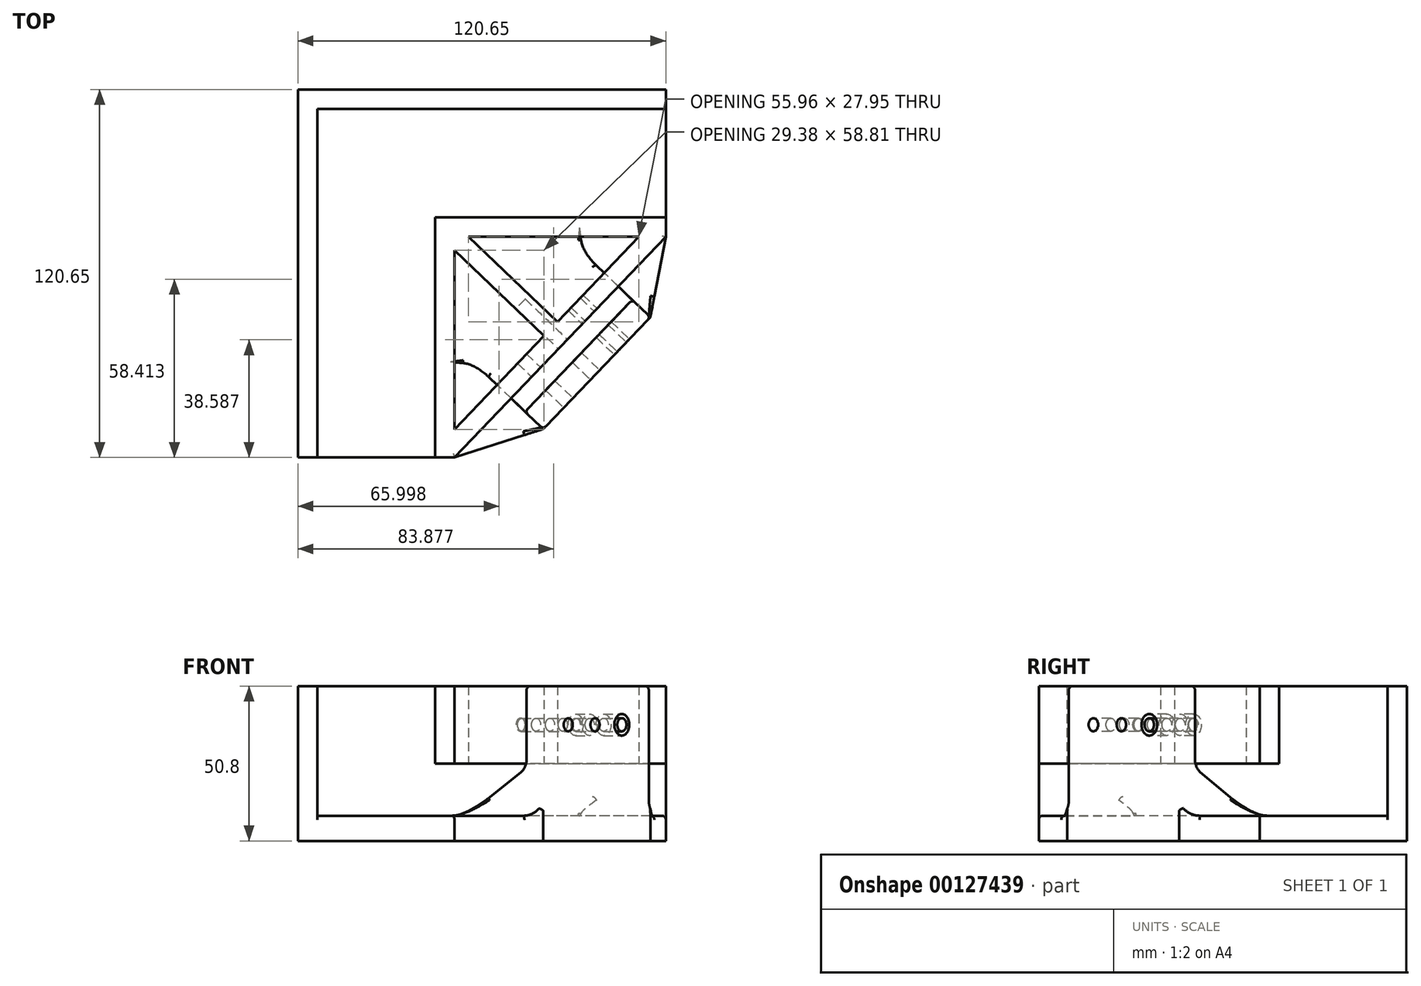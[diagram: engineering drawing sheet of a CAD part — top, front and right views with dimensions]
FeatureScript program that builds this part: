
annotation { "Feature Type Name" : "Feature", "Feature Type Description" : "" }
export const myFeature = defineFeature(function(context is Context, id is Id, definition is map)
    precondition{}
    {
        {
            var Q0;
            Q0=qCreatedBy(makeId("Top.planeOp"),FACE);
            var sketch = newSketch(context, id + "F0", { "sketchPlane" : qUnion([Q0])});
            skLineSegment(sketch, "E0", {"start": v(0, 0) * mm, "end": v(114.3, 0) * mm});
            skLineSegment(sketch, "E1", {"start": v(114.3, 0) * mm, "end": v(114.3, -35.56) * mm});
            skLineSegment(sketch, "E2", {"start": v(114.3, -35.56) * mm, "end": v(38.6, -35.56) * mm});
            skLineSegment(sketch, "E3", {"start": v(38.6, -35.56) * mm, "end": v(38.6, -114.3) * mm});
            skLineSegment(sketch, "E4", {"start": v(38.6, -114.3) * mm, "end": v(0, -114.3) * mm});
            skLineSegment(sketch, "E5", {"start": v(0, -114.3) * mm, "end": v(0, 0) * mm});
            skLineSegment(sketch, "E6.0", {"start": v(0, 6.35) * mm, "end": v(114.3, 6.35) * mm});
            skLineSegment(sketch, "E7.0", {"start": v(114.3, -41.91) * mm, "end": v(44.96, -41.91) * mm});
            skLineSegment(sketch, "E8.0", {"start": v(44.96, -41.91) * mm, "end": v(44.96, -114.3) * mm});
            skLineSegment(sketch, "E9.0", {"start": v(-6.35, -114.3) * mm, "end": v(-6.35, -12.7) * mm});
            skLineSegment(sketch, "E10", {"start": v(0, 6.35) * mm, "end": v(-6.35, 6.35) * mm});
            skLineSegment(sketch, "E11", {"start": v(-6.35, 6.35) * mm, "end": v(-6.35, -12.7) * mm});
            skLineSegment(sketch, "E12", {"start": v(0, -114.3) * mm, "end": v(-6.35, -114.3) * mm});
            skLineSegment(sketch, "E13", {"start": v(114.3, -41.91) * mm, "end": v(114.3, -35.56) * mm});
            skLineSegment(sketch, "E14", {"start": v(114.3, 0) * mm, "end": v(114.3, 6.35) * mm});
            skLineSegment(sketch, "E15", {"start": v(38.6, -114.3) * mm, "end": v(44.96, -114.3) * mm});
            skLineSegment(sketch, "E16", {"start": v(44.96, -114.3) * mm, "end": v(114.3, -41.91) * mm});
            skLineSegment(sketch, "E17.0", {"start": v(44.96, -105.12) * mm, "end": v(105.5, -41.91) * mm});
            skLineSegment(sketch, "E18", {"start": v(44.96, -41.91) * mm, "end": v(76.53, -72.16) * mm});
            skLineSegment(sketch, "E19.0", {"start": v(44.96, -46.3) * mm, "end": v(74.34, -74.45) * mm});
            skLineSegment(sketch, "E20.0", {"start": v(49.55, -41.91) * mm, "end": v(78.73, -69.86) * mm});
            skLineSegment(sketch, "E21.0", {"start": v(68.13, -99.28) * mm, "end": v(103.28, -62.6) * mm});
            skLineSegment(sketch, "E22.0", {"start": v(74.1, -105) * mm, "end": v(109.24, -68.3) * mm});
            skLineSegment(sketch, "E23", {"start": v(76.53, -72.16) * mm, "end": v(91.67, -86.65) * mm});
            skLineSegment(sketch, "E24.0", {"start": v(68.13, -99.28) * mm, "end": v(74.1, -105) * mm});
            skLineSegment(sketch, "E25.0", {"start": v(103.28, -62.6) * mm, "end": v(109.24, -68.3) * mm});
            skLineSegment(sketch, "E26", {"start": v(109.24, -68.3) * mm, "end": v(114.3, -41.91) * mm});
            skLineSegment(sketch, "E27", {"start": v(74.1, -105) * mm, "end": v(44.96, -114.3) * mm});
            skSolve(sketch);
        }
        {
            var Q0;
            Q0=makeQuery(id+"F0.imprint","IMPRINT",FACE,{"disambiguationData":[TD([[makeQuery(id+"F0.imprint","IMPRINT",EDGE,{"derivedFrom":sQuery(id+"F0.wireOp",EDGE,"E0")}),1.0]])]});
            var Q1;
            Q1=makeQuery(id+"F0.imprint","IMPRINT",FACE,{"disambiguationData":[TD([[makeQuery(id+"F0.imprint","IMPRINT",EDGE,{"derivedFrom":sQuery(id+"F0.wireOp",EDGE,"E0")}),-1.0]])]});
            var Q2;
            Q2=makeQuery(id+"F0.imprint","IMPRINT",FACE,{"disambiguationData":[TD([[makeQuery(id+"F0.imprint","IMPRINT",EDGE,{"derivedFrom":sQuery(id+"F0.wireOp",EDGE,"E2")}),1.0]])]});
            var Q3;
            {var subQ3=sQuery(id+"F0.wireOp",EDGE,"E19.0");Q3=makeQuery(id+"F0.imprint","IMPRINT",FACE,{"disambiguationData":[TD([[makeQuery(id+"F0.imprint","IMPRINT",EDGE,{"derivedFrom":subQ3}),-1.0]])]});}
            var Q4;
            {var subQ0=sQuery(id+"F0.wireOp",EDGE,"E18");Q4=makeQuery(id+"F0.imprint","IMPRINT",FACE,{"disambiguationData":[TD([[makeQuery(id+"F0.imprint","IMPRINT",EDGE,{"derivedFrom":subQ0}),-1.0]])]});}
            var Q5;
            {var subQ0=sQuery(id+"F0.wireOp",EDGE,"E18");Q5=makeQuery(id+"F0.imprint","IMPRINT",FACE,{"disambiguationData":[TD([[makeQuery(id+"F0.imprint","IMPRINT",EDGE,{"derivedFrom":subQ0}),1.0]])]});}
            var Q6;
            {var subQ3=sQuery(id+"F0.wireOp",EDGE,"E20.0");Q6=makeQuery(id+"F0.imprint","IMPRINT",FACE,{"disambiguationData":[TD([[makeQuery(id+"F0.imprint","IMPRINT",EDGE,{"derivedFrom":subQ3}),1.0]])]});}
            var Q7;
            {var subQ0=sQuery(id+"F0.wireOp",EDGE,"E16");Q7=makeQuery(id+"F0.imprint","IMPRINT",FACE,{"disambiguationData":[TD([[makeQuery(id+"F0.imprint","IMPRINT",EDGE,{"derivedFrom":subQ0}),1.0]])]});}
            var Q8;
            {var subQ0=sQuery(id+"F0.wireOp",EDGE,"E24.0");Q8=makeQuery(id+"F0.imprint","IMPRINT",FACE,{"disambiguationData":[TD([[makeQuery(id+"F0.imprint","IMPRINT",EDGE,{"derivedFrom":subQ0}),-1.0]])]});}
            var Q9;
            {var subQ0=sQuery(id+"F0.wireOp",EDGE,"E25.0");Q9=makeQuery(id+"F0.imprint","IMPRINT",FACE,{"disambiguationData":[TD([[makeQuery(id+"F0.imprint","IMPRINT",EDGE,{"derivedFrom":subQ0}),1.0]])]});}
            var Q10;
            {var subQ0=sQuery(id+"F0.wireOp",EDGE,"E24.0");Q10=makeQuery(id+"F0.imprint","IMPRINT",FACE,{"disambiguationData":[TD([[makeQuery(id+"F0.imprint","IMPRINT",EDGE,{"derivedFrom":subQ0}),1.0]])]});}
            var Q11;
            {var subQ0=sQuery(id+"F0.wireOp",EDGE,"E25.0");Q11=makeQuery(id+"F0.imprint","IMPRINT",FACE,{"disambiguationData":[TD([[makeQuery(id+"F0.imprint","IMPRINT",EDGE,{"derivedFrom":subQ0}),-1.0]])]});}
            extrude(context, id + "F1", {"entities" : qUnion([Q0, Q1, Q2, Q3, Q4, Q5, Q6, Q7, Q8, Q9, Q10, Q11]), "depth" : 8.25 * mm});
        }
        {
            var Q0;
            Q0=makeQuery(id+"F0.imprint","IMPRINT",FACE,{"disambiguationData":[TD([[makeQuery(id+"F0.imprint","IMPRINT",EDGE,{"derivedFrom":sQuery(id+"F0.wireOp",EDGE,"E0")}),1.0]])]});
            extrude(context, id + "F2", {"entities" : qUnion([Q0]), "operationType" : NewBodyOperationType.ADD, "depth" : 50.8 * mm});
        }
        {
            var Q0;
            Q0=makeQuery(id+"F0.imprint","IMPRINT",FACE,{"disambiguationData":[TD([[makeQuery(id+"F0.imprint","IMPRINT",EDGE,{"derivedFrom":sQuery(id+"F0.wireOp",EDGE,"E2")}),1.0]])]});
            var Q1;
            {var subQ1=sQuery(id+"F0.wireOp",EDGE,"E17.0");var subQ4=sQuery(id+"F0.wireOp",EDGE,"E8.0");var subQ5=makeQuery(id+"F0.imprint","INTERSECT",VERTEX,{"derivedFrom":[subQ4,subQ1]});Q1=makeQuery(id+"F0.imprint","IMPRINT",FACE,{"disambiguationData":[TD([[makeQuery(id+"F0.imprint","IMPRINT",EDGE,{"disambiguationData":[TD([[subQ5,-1.0]])],"derivedFrom":subQ1}),-1.0]])]});}
            var Q2;
            {var subQ0=sQuery(id+"F0.wireOp",EDGE,"E17.0");var subQ1=sQuery(id+"F0.wireOp",EDGE,"E7.0");var subQ2=makeQuery(id+"F0.imprint","INTERSECT",VERTEX,{"derivedFrom":[subQ1,subQ0]});Q2=makeQuery(id+"F0.imprint","IMPRINT",FACE,{"disambiguationData":[TD([[makeQuery(id+"F0.imprint","IMPRINT",EDGE,{"disambiguationData":[TD([[subQ2,1.0]])],"derivedFrom":subQ0}),-1.0]])]});}
            var Q3;
            {var subQ0=sQuery(id+"F0.wireOp",EDGE,"E18");Q3=makeQuery(id+"F0.imprint","IMPRINT",FACE,{"disambiguationData":[TD([[makeQuery(id+"F0.imprint","IMPRINT",EDGE,{"derivedFrom":subQ0}),1.0]])]});}
            var Q4;
            {var subQ0=sQuery(id+"F0.wireOp",EDGE,"E18");Q4=makeQuery(id+"F0.imprint","IMPRINT",FACE,{"disambiguationData":[TD([[makeQuery(id+"F0.imprint","IMPRINT",EDGE,{"derivedFrom":subQ0}),-1.0]])]});}
            extrude(context, id + "F3", {"entities" : qUnion([Q0, Q1, Q2, Q3, Q4]), "depth" : 50.8 * mm, "hasSecondDirection" : true, "secondDirectionOppositeDirection" : false, "secondDirectionDepth" : 25.4 * mm});
        }
        {
            var Q0;
            {var subQ0=sQuery(id+"F0.wireOp",EDGE,"E24.0");Q0=makeQuery(id+"F0.imprint","IMPRINT",FACE,{"disambiguationData":[TD([[makeQuery(id+"F0.imprint","IMPRINT",EDGE,{"derivedFrom":subQ0}),1.0]])]});}
            var Q1;
            {var subQ0=sQuery(id+"F0.wireOp",EDGE,"E25.0");Q1=makeQuery(id+"F0.imprint","IMPRINT",FACE,{"disambiguationData":[TD([[makeQuery(id+"F0.imprint","IMPRINT",EDGE,{"derivedFrom":subQ0}),-1.0]])]});}
            extrude(context, id + "F4", {"entities" : qUnion([Q0, Q1]), "depth" : 50.8 * mm});
        }
        {
            var Q0;
            Q0=makeQuery(id+"F1.opExtrude","SWEPT_BODY",BODY,{"disambiguationData":[OSD([sQuery(id+"F0.wireOp",EDGE,"E1"),sQuery(id+"F0.wireOp",EDGE,"E4"),sQuery(id+"F0.wireOp",EDGE,"E6.0"),sQuery(id+"F0.wireOp",EDGE,"E9.0"),sQuery(id+"F0.wireOp",EDGE,"E10"),sQuery(id+"F0.wireOp",EDGE,"E11"),sQuery(id+"F0.wireOp",EDGE,"E12"),sQuery(id+"F0.wireOp",EDGE,"E13"),sQuery(id+"F0.wireOp",EDGE,"E14"),sQuery(id+"F0.wireOp",EDGE,"E15"),sQuery(id+"F0.wireOp",EDGE,"E22.0"),sQuery(id+"F0.wireOp",EDGE,"E26"),sQuery(id+"F0.wireOp",EDGE,"E27")])]});
            var Q1;
            Q1=makeQuery(id+"F4.opExtrude","SWEPT_BODY",BODY,{"disambiguationData":[OSD([sQuery(id+"F0.wireOp",EDGE,"E21.0"),sQuery(id+"F0.wireOp",EDGE,"E22.0"),sQuery(id+"F0.wireOp",EDGE,"E24.0"),sQuery(id+"F0.wireOp",EDGE,"E25.0")])]});
            booleanBodies(context, id + "F5", {"operationType" : BooleanOperationType.UNION, "tools" : qUnion([Q0, Q1])});
        }
        {
            var Q0;
            Q0=makeQuery(id+"F5.opBoolean","INTERSECT",EDGE,{"derivedFrom":[makeQuery(id+"F1.opExtrude","CAP_FACE",FACE,{"disambiguationData":[OSD([sQuery(id+"F0.wireOp",EDGE,"E1"),sQuery(id+"F0.wireOp",EDGE,"E4"),sQuery(id+"F0.wireOp",EDGE,"E6.0"),sQuery(id+"F0.wireOp",EDGE,"E9.0"),sQuery(id+"F0.wireOp",EDGE,"E10"),sQuery(id+"F0.wireOp",EDGE,"E11"),sQuery(id+"F0.wireOp",EDGE,"E12"),sQuery(id+"F0.wireOp",EDGE,"E13"),sQuery(id+"F0.wireOp",EDGE,"E14"),sQuery(id+"F0.wireOp",EDGE,"E15"),sQuery(id+"F0.wireOp",EDGE,"E22.0"),sQuery(id+"F0.wireOp",EDGE,"E26"),sQuery(id+"F0.wireOp",EDGE,"E27")])],"isStart":false}),makeQuery(id+"F4.opExtrude","SWEPT_FACE",FACE,{"disambiguationData":[OSD([sQuery(id+"F0.wireOp",EDGE,"E21.0")])]})]});
            chamfer(context, id + "F6", {"entities" : qUnion([Q0]), "chamferType" : ChamferType.OFFSET_ANGLE, "width" : 15.88 * mm, "oppositeDirection" : false, "angle" : 60 * degree, "tangentPropagation" : true});
        }
        {
            var Q0;
            {var subQ0=makeQuery(id+"F4.opExtrude","SWEPT_FACE",FACE,{"disambiguationData":[OSD([sQuery(id+"F0.wireOp",EDGE,"E21.0")])]});Q0=makeQuery(id+"F6.opChamfer","BLEND_EDGE",EDGE,{"blendedFrom":[makeQuery(id+"F5.opBoolean","INTERSECT",EDGE,{"derivedFrom":[makeQuery(id+"F1.opExtrude","CAP_FACE",FACE,{"disambiguationData":[OSD([sQuery(id+"F0.wireOp",EDGE,"E1"),sQuery(id+"F0.wireOp",EDGE,"E4"),sQuery(id+"F0.wireOp",EDGE,"E6.0"),sQuery(id+"F0.wireOp",EDGE,"E9.0"),sQuery(id+"F0.wireOp",EDGE,"E10"),sQuery(id+"F0.wireOp",EDGE,"E11"),sQuery(id+"F0.wireOp",EDGE,"E12"),sQuery(id+"F0.wireOp",EDGE,"E13"),sQuery(id+"F0.wireOp",EDGE,"E14"),sQuery(id+"F0.wireOp",EDGE,"E15"),sQuery(id+"F0.wireOp",EDGE,"E22.0"),sQuery(id+"F0.wireOp",EDGE,"E26"),sQuery(id+"F0.wireOp",EDGE,"E27")])],"isStart":false}),subQ0]}),subQ0],"blendedInto":[subQ0]});}
            var Q1;
            {var subQ0=makeQuery(id+"F1.opExtrude","CAP_FACE",FACE,{"disambiguationData":[OSD([sQuery(id+"F0.wireOp",EDGE,"E1"),sQuery(id+"F0.wireOp",EDGE,"E4"),sQuery(id+"F0.wireOp",EDGE,"E6.0"),sQuery(id+"F0.wireOp",EDGE,"E9.0"),sQuery(id+"F0.wireOp",EDGE,"E10"),sQuery(id+"F0.wireOp",EDGE,"E11"),sQuery(id+"F0.wireOp",EDGE,"E12"),sQuery(id+"F0.wireOp",EDGE,"E13"),sQuery(id+"F0.wireOp",EDGE,"E14"),sQuery(id+"F0.wireOp",EDGE,"E15"),sQuery(id+"F0.wireOp",EDGE,"E22.0"),sQuery(id+"F0.wireOp",EDGE,"E26"),sQuery(id+"F0.wireOp",EDGE,"E27")])],"isStart":false});Q1=makeQuery(id+"F6.opChamfer","BLEND_EDGE",EDGE,{"blendedFrom":[makeQuery(id+"F5.opBoolean","INTERSECT",EDGE,{"derivedFrom":[subQ0,makeQuery(id+"F4.opExtrude","SWEPT_FACE",FACE,{"disambiguationData":[OSD([sQuery(id+"F0.wireOp",EDGE,"E21.0")])]})]}),subQ0],"blendedInto":[subQ0]});}
            var Q2;
            Q2=makeQuery(id+"F5.opBoolean","INTERSECT",EDGE,{"derivedFrom":[makeQuery(id+"F1.opExtrude","CAP_FACE",FACE,{"disambiguationData":[OSD([sQuery(id+"F0.wireOp",EDGE,"E1"),sQuery(id+"F0.wireOp",EDGE,"E4"),sQuery(id+"F0.wireOp",EDGE,"E6.0"),sQuery(id+"F0.wireOp",EDGE,"E9.0"),sQuery(id+"F0.wireOp",EDGE,"E10"),sQuery(id+"F0.wireOp",EDGE,"E11"),sQuery(id+"F0.wireOp",EDGE,"E12"),sQuery(id+"F0.wireOp",EDGE,"E13"),sQuery(id+"F0.wireOp",EDGE,"E14"),sQuery(id+"F0.wireOp",EDGE,"E15"),sQuery(id+"F0.wireOp",EDGE,"E22.0"),sQuery(id+"F0.wireOp",EDGE,"E26"),sQuery(id+"F0.wireOp",EDGE,"E27")])],"isStart":false}),makeQuery(id+"F4.opExtrude","SWEPT_FACE",FACE,{"disambiguationData":[OSD([sQuery(id+"F0.wireOp",EDGE,"E24.0")])]})]});
            var Q3;
            Q3=makeQuery(id+"F5.opBoolean","INTERSECT",EDGE,{"derivedFrom":[makeQuery(id+"F1.opExtrude","CAP_FACE",FACE,{"disambiguationData":[OSD([sQuery(id+"F0.wireOp",EDGE,"E1"),sQuery(id+"F0.wireOp",EDGE,"E4"),sQuery(id+"F0.wireOp",EDGE,"E6.0"),sQuery(id+"F0.wireOp",EDGE,"E9.0"),sQuery(id+"F0.wireOp",EDGE,"E10"),sQuery(id+"F0.wireOp",EDGE,"E11"),sQuery(id+"F0.wireOp",EDGE,"E12"),sQuery(id+"F0.wireOp",EDGE,"E13"),sQuery(id+"F0.wireOp",EDGE,"E14"),sQuery(id+"F0.wireOp",EDGE,"E15"),sQuery(id+"F0.wireOp",EDGE,"E22.0"),sQuery(id+"F0.wireOp",EDGE,"E26"),sQuery(id+"F0.wireOp",EDGE,"E27")])],"isStart":false}),makeQuery(id+"F4.opExtrude","SWEPT_FACE",FACE,{"disambiguationData":[OSD([sQuery(id+"F0.wireOp",EDGE,"E25.0")])]})]});
            fillet(context, id + "F7", {"entities" : qUnion([Q0, Q1, Q2, Q3]), "radius" : 5.08 * mm, "tangentPropagation" : true, "allowEdgeOverflow" : false});
        }
        {
            var Q0;
            Q0=makeQuery(id+"F6.opChamfer","BLEND_EDGE",EDGE,{"blendedFrom":[makeQuery(id+"F5.opBoolean","INTERSECT",EDGE,{"derivedFrom":[makeQuery(id+"F1.opExtrude","CAP_FACE",FACE,{"disambiguationData":[OSD([sQuery(id+"F0.wireOp",EDGE,"E1"),sQuery(id+"F0.wireOp",EDGE,"E4"),sQuery(id+"F0.wireOp",EDGE,"E6.0"),sQuery(id+"F0.wireOp",EDGE,"E9.0"),sQuery(id+"F0.wireOp",EDGE,"E10"),sQuery(id+"F0.wireOp",EDGE,"E11"),sQuery(id+"F0.wireOp",EDGE,"E12"),sQuery(id+"F0.wireOp",EDGE,"E13"),sQuery(id+"F0.wireOp",EDGE,"E14"),sQuery(id+"F0.wireOp",EDGE,"E15"),sQuery(id+"F0.wireOp",EDGE,"E22.0"),sQuery(id+"F0.wireOp",EDGE,"E26"),sQuery(id+"F0.wireOp",EDGE,"E27")])],"isStart":false}),makeQuery(id+"F4.opExtrude","SWEPT_FACE",FACE,{"disambiguationData":[OSD([sQuery(id+"F0.wireOp",EDGE,"E21.0")])]})]}),makeQuery(id+"F4.opExtrude","SWEPT_FACE",FACE,{"disambiguationData":[OSD([sQuery(id+"F0.wireOp",EDGE,"E24.0")])]})],"blendedInto":[makeQuery(id+"F4.opExtrude","SWEPT_FACE",FACE,{"disambiguationData":[OSD([sQuery(id+"F0.wireOp",EDGE,"E24.0")])]})]});
            var Q1;
            Q1=makeQuery(id+"F4.opExtrude","SWEPT_EDGE",EDGE,{"disambiguationData":[OSD([sQuery(id+"F0.wireOp",EDGE,"E22.0"),sQuery(id+"F0.wireOp",EDGE,"E24.0"),sQuery(id+"F0.wireOp",EDGE,"E27")])]});
            var Q2;
            Q2=makeQuery(id+"F4.opExtrude","CAP_EDGE",EDGE,{"disambiguationData":[OSD([sQuery(id+"F0.wireOp",EDGE,"E24.0")])],"isStart":false});
            var Q3;
            Q3=makeQuery(id+"F4.opExtrude","CAP_EDGE",EDGE,{"disambiguationData":[OSD([sQuery(id+"F0.wireOp",EDGE,"E22.0")])],"isStart":false});
            var Q4;
            Q4=makeQuery(id+"F4.opExtrude","CAP_EDGE",EDGE,{"disambiguationData":[OSD([sQuery(id+"F0.wireOp",EDGE,"E21.0")])],"isStart":false});
            var Q5;
            Q5=makeQuery(id+"F4.opExtrude","CAP_EDGE",EDGE,{"disambiguationData":[OSD([sQuery(id+"F0.wireOp",EDGE,"E25.0")])],"isStart":false});
            var Q6;
            Q6=makeQuery(id+"F4.opExtrude","SWEPT_EDGE",EDGE,{"disambiguationData":[OSD([sQuery(id+"F0.wireOp",EDGE,"E21.0"),sQuery(id+"F0.wireOp",EDGE,"E25.0")])]});
            var Q7;
            Q7=makeQuery(id+"F4.opExtrude","SWEPT_EDGE",EDGE,{"disambiguationData":[OSD([sQuery(id+"F0.wireOp",EDGE,"E22.0"),sQuery(id+"F0.wireOp",EDGE,"E25.0"),sQuery(id+"F0.wireOp",EDGE,"E26")])]});
            var Q8;
            Q8=makeQuery(id+"F1.opExtrude","CAP_EDGE",EDGE,{"disambiguationData":[OSD([sQuery(id+"F0.wireOp",EDGE,"E27")])],"isStart":false});
            var Q9;
            Q9=makeQuery(id+"F1.opExtrude","CAP_EDGE",EDGE,{"disambiguationData":[OSD([sQuery(id+"F0.wireOp",EDGE,"E4"),sQuery(id+"F0.wireOp",EDGE,"E12"),sQuery(id+"F0.wireOp",EDGE,"E15")])],"isStart":false});
            var Q10;
            Q10=makeQuery(id+"F1.opExtrude","CAP_EDGE",EDGE,{"disambiguationData":[OSD([sQuery(id+"F0.wireOp",EDGE,"E26")])],"isStart":false});
            var Q11;
            Q11=makeQuery(id+"F1.opExtrude","CAP_EDGE",EDGE,{"disambiguationData":[OSD([sQuery(id+"F0.wireOp",EDGE,"E1"),sQuery(id+"F0.wireOp",EDGE,"E13"),sQuery(id+"F0.wireOp",EDGE,"E14")])],"isStart":false});
            fillet(context, id + "F8", {"entities" : qUnion([Q0, Q1, Q2, Q3, Q4, Q5, Q6, Q7, Q8, Q9, Q10, Q11]), "radius" : 1.27 * mm, "tangentPropagation" : true, "allowEdgeOverflow" : false});
        }
        {
            var Q0;
            {var subQ0=sQuery(id+"F0.wireOp",EDGE,"E22.0");Q0=makeQuery(id+"F5.opBoolean","MERGE",FACE,{"derivedFrom":[makeQuery(id+"F1.opExtrude","SWEPT_FACE",FACE,{"disambiguationData":[OSD([subQ0])]}),makeQuery(id+"F4.opExtrude","SWEPT_FACE",FACE,{"disambiguationData":[OSD([subQ0])]})]});}
            cPlane(context, id + "F9", {"entities" : qUnion([Q0]), "cplaneType" : CPlaneType.OFFSET, "offset" : 25.4 * mm, "width" : 152.4 * mm, "height" : 152.4 * mm});
        }
        {
            var Q0;
            Q0=qCreatedBy(id+"F9.planeOp",FACE);
            var sketch = newSketch(context, id + "F10", { "sketchPlane" : qUnion([Q0])});
            skCircle(sketch, "E28", {"center": v(0, 38.1) * mm, "radius": 2.16 * mm});
            skCircle(sketch, "E29", {"center": v(0, 38.1) * mm, "radius": 3.56 * mm});
            skLineSegment(sketch, "E30", {"start": v(6.35, 0) * mm, "end": v(6.35, 5.08) * mm});
            skCircle(sketch, "E31.MirrorC", {"center": v(12.7, 38.1) * mm, "radius": 3.56 * mm});
            skCircle(sketch, "E32.MirrorC", {"center": v(12.7, 38.1) * mm, "radius": 2.16 * mm});
            skLineSegment(sketch, "E33", {"start": v(0, 0) * mm, "end": v(0, 5.08) * mm});
            skCircle(sketch, "E34.MirrorC", {"center": v(-12.7, 38.1) * mm, "radius": 2.16 * mm});
            skCircle(sketch, "E35.MirrorC", {"center": v(-12.7, 38.1) * mm, "radius": 3.56 * mm});
            skSolve(sketch);
        }
        {
            var Q0;
            Q0=makeQuery(id+"F10.imprint","IMPRINT",FACE,{"disambiguationData":[TD([[makeQuery(id+"F10.imprint","IMPRINT",EDGE,{"derivedFrom":sQuery(id+"F10.wireOp",EDGE,"E34.MirrorC")}),1.0]])]});
            var Q1;
            Q1=makeQuery(id+"F10.imprint","IMPRINT",FACE,{"disambiguationData":[TD([[makeQuery(id+"F10.imprint","IMPRINT",EDGE,{"derivedFrom":sQuery(id+"F10.wireOp",EDGE,"E28")}),1.0]])]});
            var Q2;
            Q2=makeQuery(id+"F10.imprint","IMPRINT",FACE,{"disambiguationData":[TD([[makeQuery(id+"F10.imprint","IMPRINT",EDGE,{"derivedFrom":sQuery(id+"F10.wireOp",EDGE,"E32.MirrorC")}),-1.0]])]});
            extrude(context, id + "F11", {"entities" : qUnion([Q0, Q1, Q2]), "oppositeDirection" : true, "depth" : 59.17 * mm});
        }
        {
            var Q0;
            Q0=makeQuery(id+"F11.opExtrude","SWEPT_BODY",BODY,{"disambiguationData":[OSD([sQuery(id+"F10.wireOp",EDGE,"E32.MirrorC")])]});
            var Q1;
            Q1=makeQuery(id+"F11.opExtrude","SWEPT_BODY",BODY,{"disambiguationData":[OSD([sQuery(id+"F10.wireOp",EDGE,"E28")])]});
            var Q2;
            Q2=makeQuery(id+"F11.opExtrude","SWEPT_BODY",BODY,{"disambiguationData":[OSD([sQuery(id+"F10.wireOp",EDGE,"E34.MirrorC")])]});
            var Q3;
            Q3=makeQuery(id+"F1.opExtrude","SWEPT_BODY",BODY,{"disambiguationData":[OSD([sQuery(id+"F0.wireOp",EDGE,"E1"),sQuery(id+"F0.wireOp",EDGE,"E4"),sQuery(id+"F0.wireOp",EDGE,"E6.0"),sQuery(id+"F0.wireOp",EDGE,"E9.0"),sQuery(id+"F0.wireOp",EDGE,"E10"),sQuery(id+"F0.wireOp",EDGE,"E11"),sQuery(id+"F0.wireOp",EDGE,"E12"),sQuery(id+"F0.wireOp",EDGE,"E13"),sQuery(id+"F0.wireOp",EDGE,"E14"),sQuery(id+"F0.wireOp",EDGE,"E15"),sQuery(id+"F0.wireOp",EDGE,"E22.0"),sQuery(id+"F0.wireOp",EDGE,"E26"),sQuery(id+"F0.wireOp",EDGE,"E27")])]});
            var Q4;
            Q4=makeQuery(id+"F3.opExtrude","SWEPT_BODY",BODY,{"disambiguationData":[OSD([sQuery(id+"F0.wireOp",EDGE,"E2"),sQuery(id+"F0.wireOp",EDGE,"E3"),sQuery(id+"F0.wireOp",EDGE,"E7.0"),sQuery(id+"F0.wireOp",EDGE,"E8.0"),sQuery(id+"F0.wireOp",EDGE,"E13"),sQuery(id+"F0.wireOp",EDGE,"E15"),sQuery(id+"F0.wireOp",EDGE,"E16"),sQuery(id+"F0.wireOp",EDGE,"E17.0"),sQuery(id+"F0.wireOp",EDGE,"E19.0"),sQuery(id+"F0.wireOp",EDGE,"E20.0")])]});
            booleanBodies(context, id + "F12", {"operationType" : BooleanOperationType.SUBTRACTION, "tools" : qUnion([Q0, Q1, Q2]), "targets" : qUnion([Q3, Q4])});
        }
    });
